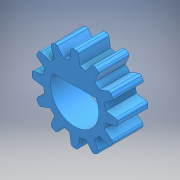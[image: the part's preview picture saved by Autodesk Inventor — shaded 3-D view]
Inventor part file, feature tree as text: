
AUTODESK INVENTOR PART (.ipt)
format: ipt  version: 2018 (Build 220112000, 112)  size: 204,800 bytes
history: native  units: mm
features: extrude x3, sketch x1, fillet x1, pattern_circular x1
ambient origin geometry x8: Origin, YZ Plane, XZ Plane, XY Plane, X Axis, Y Axis, Z Axis, Center Point
bodies: Solid1 (feature_tree)
feature tree (6):
  sketch  "Sketch1"  dims[d1=11.2mm d2=8.3mm d3=0.9mm d4=1.35mm d5=4.0mm d6=0.0mm d7=4.0mm d8=0.0mm d9=120.0mm d10=360.0deg d12=0.3mm d13=6.0mm d14=4.0mm d15=0.0mm d16=0.15mm d17=1.48mm]
  extrude  "Extrusion1"  Depth=4.0mm
  extrude  "Extrusion2"  Depth=4.0mm
  fillet  "Fillet1"  Radius=1.35mm
  pattern_circular  "Circular Pattern1"  [2 undecoded]
  extrude  "Extrusion3"  Depth=4.0mm TaperAngle=0.0deg
note: 2 required parameter values undecoded (feature->parameter linkage not recoverable at this tier; creation-order binding heuristic only, values carry confidence <= 0.55)
